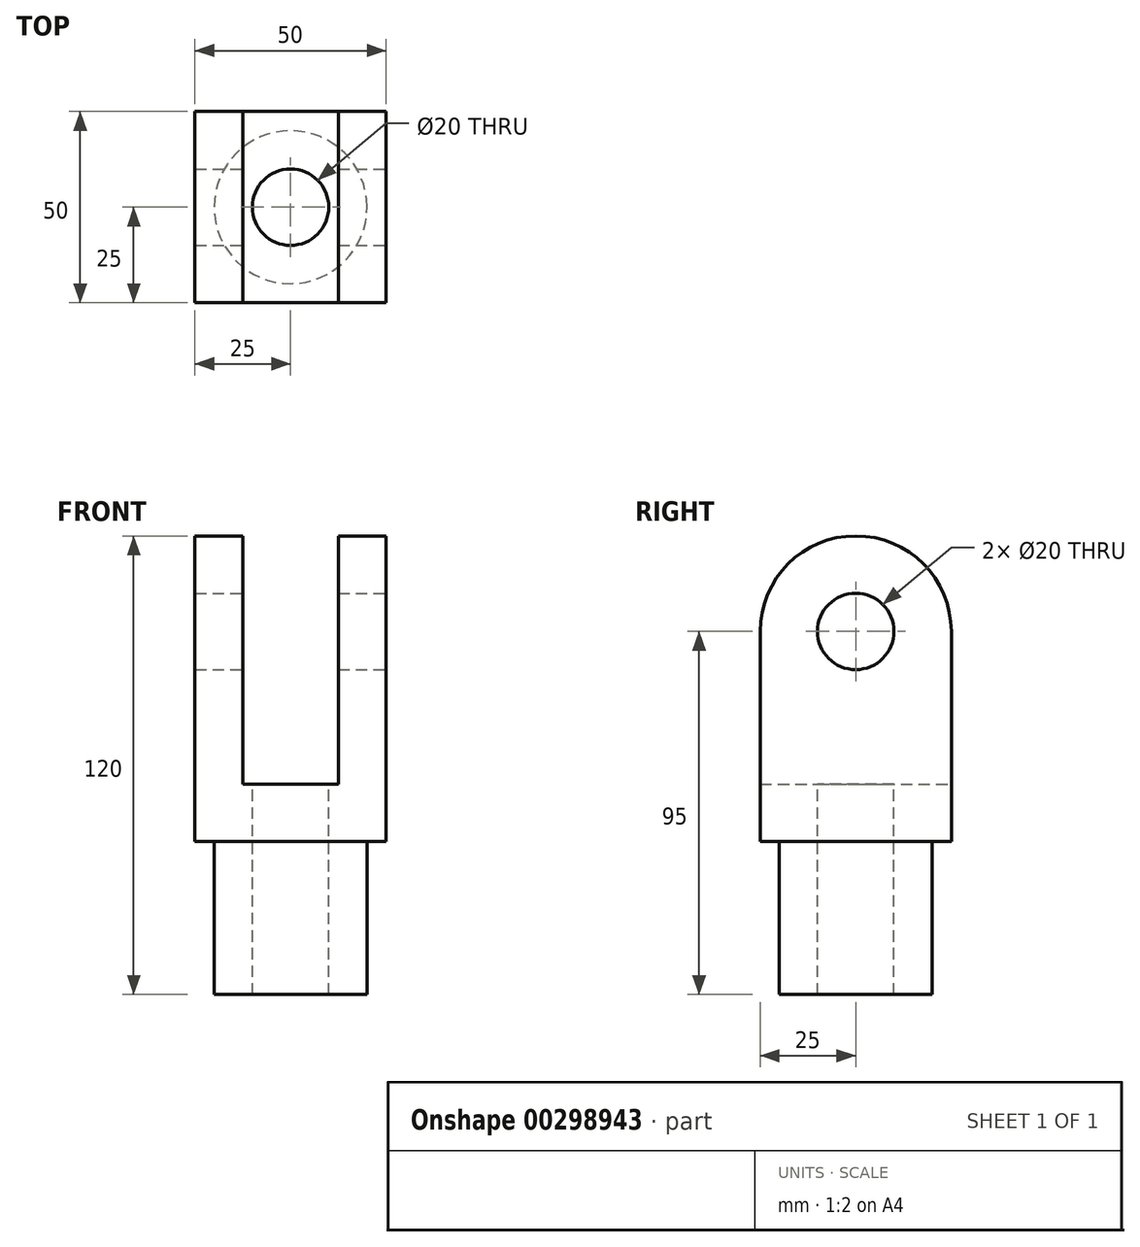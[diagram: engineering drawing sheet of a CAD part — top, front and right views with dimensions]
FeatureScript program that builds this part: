
annotation { "Feature Type Name" : "Feature", "Feature Type Description" : "" }
export const myFeature = defineFeature(function(context is Context, id is Id, definition is map)
    precondition{}
    {
        {
            var Q0;
            Q0=qCreatedBy(makeId("Front.planeOp"),FACE);
            var sketch = newSketch(context, id + "F0", { "sketchPlane" : qUnion([Q0])});
            skLineSegment(sketch, "E0", {"start": v(-25, 0) * mm, "end": v(-25, 80) * mm});
            skLineSegment(sketch, "E1", {"start": v(-25, 80) * mm, "end": v(-12.5, 80) * mm});
            skLineSegment(sketch, "E2", {"start": v(-12.5, 80) * mm, "end": v(-12.5, 15) * mm});
            skLineSegment(sketch, "E3", {"start": v(-12.5, 15) * mm, "end": v(0, 15) * mm});
            skLineSegment(sketch, "E4.MirrorCS", {"start": v(12.5, 80) * mm, "end": v(12.5, 15) * mm});
            skLineSegment(sketch, "E5.MirrorCS", {"start": v(25, 80) * mm, "end": v(12.5, 80) * mm});
            skLineSegment(sketch, "E6.MirrorCS", {"start": v(12.5, 15) * mm, "end": v(0, 15) * mm});
            skLineSegment(sketch, "E7.MirrorCS", {"start": v(25, 0) * mm, "end": v(25, 80) * mm});
            skLineSegment(sketch, "E8", {"start": v(-25, 0) * mm, "end": v(25, 0) * mm});
            skSolve(sketch);
        }
        {
            var Q0;
            Q0 = qSketchRegion(id + "F0", true);
            extrude(context, id + "F1", {"entities" : qUnion([Q0]), "depth" : 50 * mm});
        }
        {
            var Q0;
            Q0=makeQuery(id+"F1.opExtrude","SWEPT_FACE",FACE,{"disambiguationData":[OSD([sQuery(id+"F0.wireOp",EDGE,"E8")])]});
            var sketch = newSketch(context, id + "F2", { "sketchPlane" : qUnion([Q0])});
            skPoint(sketch, "E9.positionSnap0", {"position": v(0, 50) * mm});
            skCircle(sketch, "E10", {"center": v(0, 25) * mm, "radius": 20 * mm});
            skSolve(sketch);
        }
        {
            var Q0;
            Q0=makeQuery(id+"F2.imprint","IMPRINT",FACE,{"disambiguationData":[TD([[makeQuery(id+"F2.imprint","IMPRINT",EDGE,{"derivedFrom":sQuery(id+"F2.wireOp",EDGE,"E10")}),1.0]])]});
            extrude(context, id + "F3", {"entities" : qUnion([Q0]), "operationType" : NewBodyOperationType.ADD, "depth" : 40 * mm});
        }
        {
            var Q0;
            Q0=makeQuery(id+"F1.opExtrude","SWEPT_FACE",FACE,{"disambiguationData":[OSD([sQuery(id+"F0.wireOp",EDGE,"E7.MirrorCS")])]});
            var sketch = newSketch(context, id + "F4", { "sketchPlane" : qUnion([Q0])});
            skPoint(sketch, "E11", {"position": v(-25, 55) * mm});
            skCircle(sketch, "E12", {"center": v(-25, 55) * mm, "radius": 10 * mm});
            skArc(sketch, "E13", {"start": v(0, 54.63) * mm, "mid": v(-25, 79.63) * mm, "end": v(-50, 54.63) * mm});
            skSolve(sketch);
        }
        {
            var Q0;
            Q0=sQuery(id+"F4.wireOp",VERTEX,"E11");
            var Q1;
            Q1=makeQuery(id+"F1.opExtrude","SWEPT_BODY",BODY,{"disambiguationData":[OSD([sQuery(id+"F0.wireOp",EDGE,"E0"),sQuery(id+"F0.wireOp",EDGE,"E1"),sQuery(id+"F0.wireOp",EDGE,"E2"),sQuery(id+"F0.wireOp",EDGE,"E3"),sQuery(id+"F0.wireOp",EDGE,"E4.MirrorCS"),sQuery(id+"F0.wireOp",EDGE,"E5.MirrorCS"),sQuery(id+"F0.wireOp",EDGE,"E6.MirrorCS"),sQuery(id+"F0.wireOp",EDGE,"E7.MirrorCS"),sQuery(id+"F0.wireOp",EDGE,"E8")])]});
            hole(context, id + "F5", {"style" : HoleStyle.SIMPLE, "endStyle" : HoleEndStyle.THROUGH, "holeDiameter" : 20 * mm, "tappedDepth" : 12 * mm, "tapClearance" : 3, "locations" : qUnion([Q0]), "scope" : qUnion([Q1])});
        }
        {
            var Q0;
            Q0=makeQuery(id+"F1.opExtrude","CAP_EDGE",EDGE,{"disambiguationData":[OSD([sQuery(id+"F0.wireOp",EDGE,"E5.MirrorCS")])],"isStart":false});
            var Q1;
            Q1=makeQuery(id+"F1.opExtrude","CAP_EDGE",EDGE,{"disambiguationData":[OSD([sQuery(id+"F0.wireOp",EDGE,"E5.MirrorCS")])],"isStart":true});
            var Q2;
            Q2=makeQuery(id+"F1.opExtrude","CAP_EDGE",EDGE,{"disambiguationData":[OSD([sQuery(id+"F0.wireOp",EDGE,"E1")])],"isStart":false});
            var Q3;
            Q3=makeQuery(id+"F1.opExtrude","CAP_EDGE",EDGE,{"disambiguationData":[OSD([sQuery(id+"F0.wireOp",EDGE,"E1")])],"isStart":true});
            fillet(context, id + "F6", {"entities" : qUnion([Q0, Q1, Q2, Q3]), "radius" : 25 * mm, "tangentPropagation" : true, "allowEdgeOverflow" : false});
        }
        {
            var Q0;
            Q0=makeQuery(id+"F2.imprint","IMPRINT",FACE,{"disambiguationData":[TD([[makeQuery(id+"F2.imprint","IMPRINT",EDGE,{"derivedFrom":sQuery(id+"F2.wireOp",EDGE,"E10")}),-1.0]])]});
            var sketch = newSketch(context, id + "F7", { "sketchPlane" : qUnion([Q0])});
            skPoint(sketch, "E14", {"position": v(0, 25) * mm});
            skSolve(sketch);
        }
        {
            var Q0;
            Q0=sQuery(id+"F7.wireOp",VERTEX,"E14");
            var Q1;
            Q1=makeQuery(id+"F1.opExtrude","SWEPT_BODY",BODY,{"disambiguationData":[OSD([sQuery(id+"F0.wireOp",EDGE,"E0"),sQuery(id+"F0.wireOp",EDGE,"E1"),sQuery(id+"F0.wireOp",EDGE,"E2"),sQuery(id+"F0.wireOp",EDGE,"E3"),sQuery(id+"F0.wireOp",EDGE,"E4.MirrorCS"),sQuery(id+"F0.wireOp",EDGE,"E5.MirrorCS"),sQuery(id+"F0.wireOp",EDGE,"E6.MirrorCS"),sQuery(id+"F0.wireOp",EDGE,"E7.MirrorCS"),sQuery(id+"F0.wireOp",EDGE,"E8")])]});
            hole(context, id + "F8", {"style" : HoleStyle.SIMPLE, "endStyle" : HoleEndStyle.THROUGH, "oppositeDirection" : true, "holeDiameter" : 20 * mm, "tappedDepth" : 12 * mm, "tapClearance" : 3, "locations" : qUnion([Q0]), "scope" : qUnion([Q1])});
        }
        {
            var Q0;
            Q0=makeQuery(id+"F1.opExtrude","SWEPT_FACE",FACE,{"disambiguationData":[OSD([sQuery(id+"F0.wireOp",EDGE,"E3"),sQuery(id+"F0.wireOp",EDGE,"E6.MirrorCS")])]});
            var sketch = newSketch(context, id + "F9", { "sketchPlane" : qUnion([Q0])});
            skPoint(sketch, "E15", {"position": v(0, -25) * mm});
            skSolve(sketch);
        }
        {
            var Q0;
            Q0=sQuery(id+"F9.wireOp",VERTEX,"E15");
            var Q1;
            Q1=makeQuery(id+"F1.opExtrude","SWEPT_BODY",BODY,{"disambiguationData":[OSD([sQuery(id+"F0.wireOp",EDGE,"E0"),sQuery(id+"F0.wireOp",EDGE,"E1"),sQuery(id+"F0.wireOp",EDGE,"E2"),sQuery(id+"F0.wireOp",EDGE,"E3"),sQuery(id+"F0.wireOp",EDGE,"E4.MirrorCS"),sQuery(id+"F0.wireOp",EDGE,"E5.MirrorCS"),sQuery(id+"F0.wireOp",EDGE,"E6.MirrorCS"),sQuery(id+"F0.wireOp",EDGE,"E7.MirrorCS"),sQuery(id+"F0.wireOp",EDGE,"E8")])]});
            hole(context, id + "F10", {"style" : HoleStyle.SIMPLE, "endStyle" : HoleEndStyle.THROUGH, "holeDiameter" : 20 * mm, "tappedDepth" : 12 * mm, "tapClearance" : 3, "locations" : qUnion([Q0]), "scope" : qUnion([Q1])});
        }
    });
